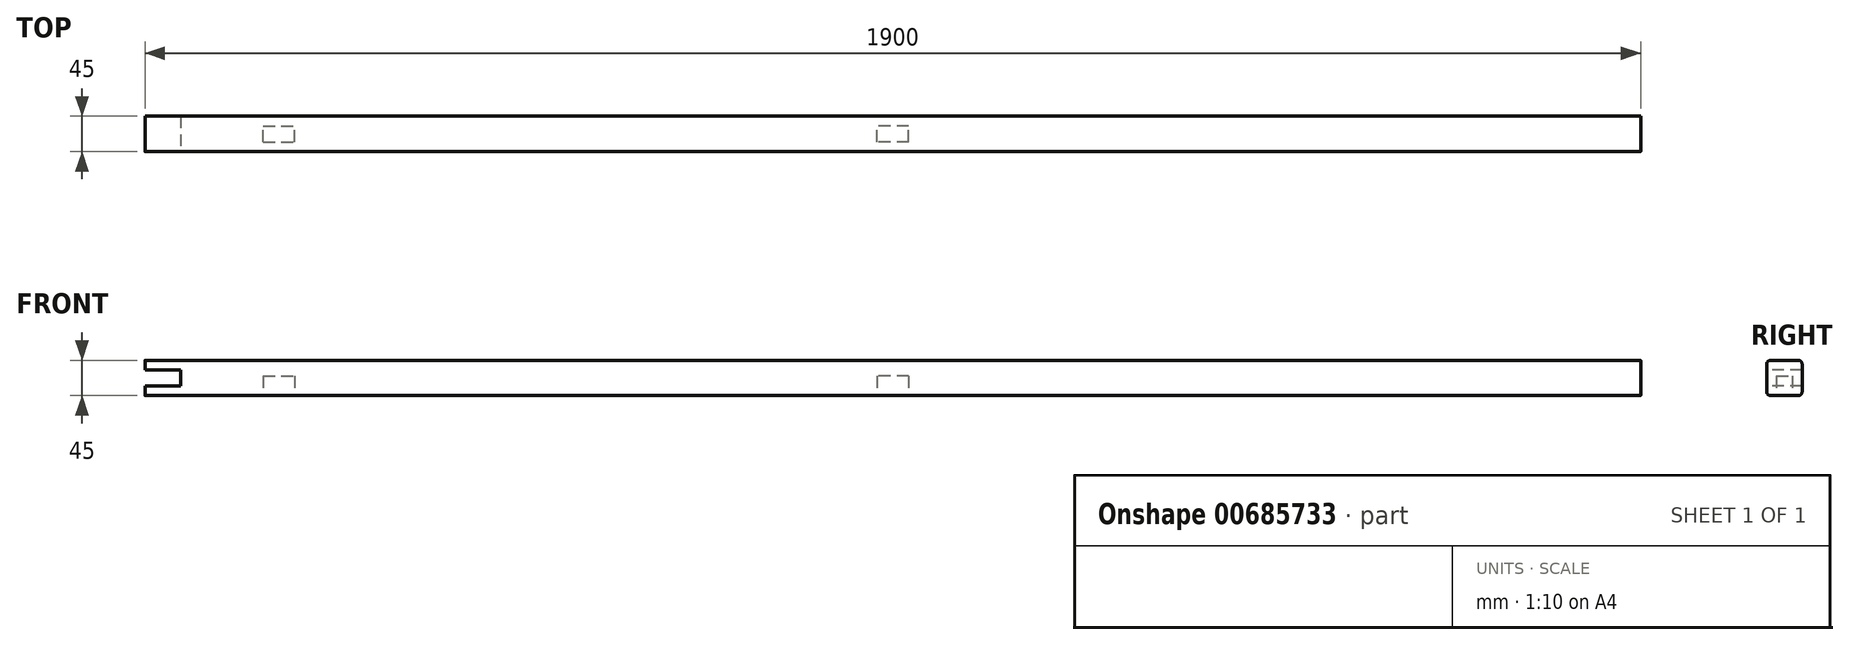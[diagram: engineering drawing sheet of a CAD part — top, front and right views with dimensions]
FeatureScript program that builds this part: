
annotation { "Feature Type Name" : "Feature", "Feature Type Description" : "" }
export const myFeature = defineFeature(function(context is Context, id is Id, definition is map)
    precondition{}
    {
        {
            var Q0;
            Q0=qCreatedBy(makeId("Right.planeOp"),FACE);
            var sketch = newSketch(context, id + "F0", { "sketchPlane" : qUnion([Q0])});
            skLineSegment(sketch, "E0.bottom", {"start": v(0, 0) * mm, "end": v(45, 0) * mm});
            skLineSegment(sketch, "E0.top", {"start": v(0, 45) * mm, "end": v(45, 45) * mm});
            skLineSegment(sketch, "E0.left", {"start": v(0, 0) * mm, "end": v(0, 45) * mm});
            skLineSegment(sketch, "E0.right", {"start": v(45, 0) * mm, "end": v(45, 45) * mm});
            skSolve(sketch);
        }
        {
            var Q0;
            Q0=qSketchRegion(id+"F0",true);
            extrude(context, id + "F1", {"entities" : qUnion([Q0]), "endBound" : BoundingType.SYMMETRIC, "depth" : 1900 * mm, "offsetDistance" : 25 * mm});
        }
        {
            var Q0;
            Q0=makeQuery(id+"F1.opExtrude","SWEPT_EDGE",EDGE,{"disambiguationData":[OSD([sQuery(id+"F0.wireOp",EDGE,"E0.top"),sQuery(id+"F0.wireOp",EDGE,"E0.left")])]});
            var Q1;
            Q1=makeQuery(id+"F1.opExtrude","SWEPT_EDGE",EDGE,{"disambiguationData":[OSD([sQuery(id+"F0.wireOp",EDGE,"E0.top"),sQuery(id+"F0.wireOp",EDGE,"E0.right")])]});
            var Q2;
            Q2=makeQuery(id+"F1.opExtrude","SWEPT_EDGE",EDGE,{"disambiguationData":[OSD([sQuery(id+"F0.wireOp",EDGE,"E0.bottom"),sQuery(id+"F0.wireOp",EDGE,"E0.left")])]});
            var Q3;
            Q3=makeQuery(id+"F1.opExtrude","SWEPT_EDGE",EDGE,{"disambiguationData":[OSD([sQuery(id+"F0.wireOp",EDGE,"E0.bottom"),sQuery(id+"F0.wireOp",EDGE,"E0.right")])]});
            fillet(context, id + "F2", {"entities" : qUnion([Q0, Q1, Q2, Q3]), "radius" : 5 * mm, "tangentPropagation" : true, "allowEdgeOverflow" : false});
        }
        {
            var Q0;
            Q0=makeQuery(id+"F1.opExtrude","SWEPT_FACE",FACE,{"disambiguationData":[OSD([sQuery(id+"F0.wireOp",EDGE,"E0.left")])]});
            var sketch = newSketch(context, id + "F3", { "sketchPlane" : qUnion([Q0])});
            skLineSegment(sketch, "E1", {"start": v(-950, 22.5) * mm, "end": v(-905, 22.5) * mm, "construction": true});
            skLineSegment(sketch, "E2.bottom", {"start": v(-905, 12.5) * mm, "end": v(-950, 12.5) * mm});
            skLineSegment(sketch, "E2.top", {"start": v(-905, 32.5) * mm, "end": v(-950, 32.5) * mm});
            skLineSegment(sketch, "E2.left", {"start": v(-905, 12.5) * mm, "end": v(-905, 32.5) * mm});
            skLineSegment(sketch, "E2.right", {"start": v(-950, 12.5) * mm, "end": v(-950, 32.5) * mm});
            skPoint(sketch, "E2.middle", {"position": v(-927.5, 22.5) * mm});
            skSolve(sketch);
        }
        {
            var Q0;
            Q0=qSketchRegion(id+"F3",true);
            extrude(context, id + "F4", {"entities" : qUnion([Q0]), "operationType" : NewBodyOperationType.REMOVE, "endBound" : BoundingType.THROUGH_ALL, "oppositeDirection" : true, "depth" : 25 * mm, "offsetDistance" : 25 * mm});
        }
        {
            var Q0;
            Q0=makeQuery(id+"F1.opExtrude","SWEPT_FACE",FACE,{"disambiguationData":[OSD([sQuery(id+"F0.wireOp",EDGE,"E0.bottom")])]});
            var sketch = newSketch(context, id + "F5", { "sketchPlane" : qUnion([Q0])});
            skLineSegment(sketch, "E3.bottom", {"start": v(-800, -12.5) * mm, "end": v(-760, -12.5) * mm});
            skLineSegment(sketch, "E3.top", {"start": v(-800, -32.5) * mm, "end": v(-760, -32.5) * mm});
            skLineSegment(sketch, "E3.left", {"start": v(-800, -12.5) * mm, "end": v(-800, -32.5) * mm});
            skLineSegment(sketch, "E3.right", {"start": v(-760, -12.5) * mm, "end": v(-760, -32.5) * mm});
            skPoint(sketch, "E3.middle", {"position": v(-780, -22.5) * mm});
            skPoint(sketch, "E3.middle.positionSnap0", {"position": v(-950, -22.5) * mm});
            skPoint(sketch, "E3.centerSnap0", {"position": v(-950, -22.5) * mm});
            skSolve(sketch);
        }
        {
            var Q0;
            Q0=qSketchRegion(id+"F5",true);
            extrude(context, id + "F6", {"entities" : qUnion([Q0]), "operationType" : NewBodyOperationType.REMOVE, "oppositeDirection" : true, "depth" : 25 * mm, "offsetDistance" : 25 * mm});
        }
        {
            var Q0;
            Q0=makeQuery(id+"F1.opExtrude","SWEPT_FACE",FACE,{"disambiguationData":[OSD([sQuery(id+"F0.wireOp",EDGE,"E0.bottom")])]});
            var sketch = newSketch(context, id + "F7", { "sketchPlane" : qUnion([Q0])});
            skLineSegment(sketch, "E4.bottom", {"start": v(20, -12.5) * mm, "end": v(-20, -12.5) * mm});
            skLineSegment(sketch, "E4.top", {"start": v(20, -32.5) * mm, "end": v(-20, -32.5) * mm});
            skLineSegment(sketch, "E4.left", {"start": v(20, -12.5) * mm, "end": v(20, -32.5) * mm});
            skLineSegment(sketch, "E4.right", {"start": v(-20, -12.5) * mm, "end": v(-20, -32.5) * mm});
            skPoint(sketch, "E4.middle", {"position": v(0, -22.5) * mm});
            skLineSegment(sketch, "E5", {"start": v(950, -22.5) * mm, "end": v(-950, -22.5) * mm, "construction": true});
            skSolve(sketch);
        }
        {
            var Q0;
            Q0=qSketchRegion(id+"F7",true);
            extrude(context, id + "F8", {"entities" : qUnion([Q0]), "operationType" : NewBodyOperationType.REMOVE, "oppositeDirection" : true, "depth" : 25 * mm, "offsetDistance" : 25 * mm});
        }
    });
